# Revit family: Door_Sliding_AssaAbloy_AllGlass-BiPart
name_source: partatom
category: Doors
units: mm (PartAtom-declared; Revit-internal decimal feet)

## family parameters
Always vertical = Yes
Cut with Voids When Loaded = No
Host = Wall
OmniClass Number = 23.30.10.17.11
OmniClass Title = Sliding Doors
Room Calculation Point = No
Shared = No

## types (4) — shared parameters
Assembly Code = B2030110
Construction Details = http://www.arcat.com
Fire Rating = As Specified
Frame Thickness = 0' - 4 1/2"
Function = Interior
Green Building-LEED = http://www.arcat.com
Height = 7' - 5 3/4"
Installation-Fabrication = http://www.besam-usa.com
Jamb Width = 0' - 1 3/4"
Keynote = 08463
Manufacturer = ASSA ABLOY Entrance Systems
Manufacturer Fax = 704-290-5555
Manufacturer Website = http://www.besam-usa.com
Panel Thickness = 0' - 1 7/8"
Product Data = http://www.arcat.com
Product Properties = http://www.besam-usa.com
RO Offset = 0' - 0 1/4"
Rough Height = 7' - 6"
Sales Information = http://www.besam-usa.com
Send Message = http://www.arcat.com
SpecWizard = http://www.arcat.com
Specification = http://www.arcat.com
Standards Conformance = as Specified
Thickness = 0' - 0"
URL = http://www.besam-usa.com
Wall Closure = By host
zero-valued in all types: Expected Lifespan (Years), Maintenance Schedule (Months), Warranty Duration (Years)

## per-type parameters (varying)
| type | Clear Opening Width | Description | Model | Panel Width | Rough Width | Width |
| FSL 16 ft | 6' - 10 1/8" | ASSA ABLOY All Glass BiPart Sliding Door - Besam SL500 CGL BP FSL16 as Specified | Besam SL500 CGL BP FSL16 | 3' - 11 7/8" | 16' - 0 1/2" | 16' - 0" |
| FSL 14 ft | 5' - 10 1/8" | ASSA ABLOY All Glass BiPart Sliding Door - Besam SL500 CGL BP FSL14 as Specified | Besam SL500 CGL BP FSL14 | 3' - 5 7/8" | 14' - 0 1/2" | 14' - 0" |
| FSL 12 ft | 4' - 10 1/8" | ASSA ABLOY All Glass BiPart Sliding Door - Besam SL500 CGL BP FSL12 as Specified | Besam SL500 CGL BP FSL12 | 2' - 11 7/8" | 12' - 0 1/2" | 12' - 0" |
| FSL 10 ft | 3' - 10 1/8" | ASSA ABLOY All Glass BiPart Sliding Door - Besam SL500 CGL BP FSL10 as Specified | Besam SL500 CGL BP FSL10 | 2' - 5 7/8" | 10' - 0 1/2" | 10' - 0" |

## geometry (parser evidence)
native form markers: Blend x6, Sweep x7
no freeform markers — native parametric forms only
